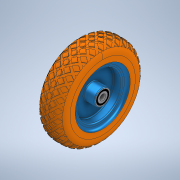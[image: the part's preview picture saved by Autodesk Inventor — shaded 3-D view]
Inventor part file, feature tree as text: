
AUTODESK INVENTOR PART (.ipt)
format: ipt  version: 2021 (Build 250183000, 183)  size: 4,260,352 bytes
history: native  units: mm
features: extrude x13, sketch x8, fillet x6, pattern_circular x2, plane x1
ambient origin geometry x8: Origin, YZ Plane, XZ Plane, XY Plane, X Axis, Y Axis, Z Axis, Center Point
bodies: Solid1 (feature_tree)
feature tree (30):
  sketch  "Sketch1"  dims[d2=70.0mm d3=0.0mm d4=8.0mm d5=0.0mm]
  extrude  "Extrusion1"  Depth=8.0mm TaperAngle=0.0deg
  extrude  "Extrusion2"  Depth=8.0mm TaperAngle=0.0deg
  extrude  "Extrusion3"  Depth=45.0mm
  sketch  "Sketch2"  dims[d6=30.0mm d7=0.0mm d8=8.0mm d9=0.0mm]
  extrude  "Extrusion4"  Depth=30.0mm TaperAngle=0.0deg
  extrude  "Extrusion5"  Depth=8.0mm
  extrude  "Extrusion6"  Depth=30.0mm
  extrude  "Extrusion7"  Depth=1.0mm
  fillet  "Fillet1"  Radius=40.0mm
  fillet  "Fillet2"  Radius=1.0mm
  fillet  "Fillet3"  Radius=27.0mm
  fillet  "Fillet4"  Radius=36.0mm
  extrude  "Extrusion8"  Depth=27.0mm
  fillet  "Fillet5"  Radius=36.0mm
  pattern_circular  "Circular Pattern1"  [2 undecoded]
  fillet  "Fillet6"  Radius=240.0mm
  extrude  "Extrusion9"  Depth=130.0mm
  extrude  "Extrusion10"  TaperAngle=45.0deg  [1 undecoded]
  plane  "Work Plane1"
  sketch  "Sketch8"  dims[d22=5.0mm d23=0.0mm d24=1.0mm d25=40.0mm d26=360.0deg d28=1.0mm d29=27.0mm d31=36.0mm]
  extrude  "Extrusion16"  Depth=2.0mm TaperAngle=0.0deg
  extrude  "Extrusion17"  Depth=2.0mm TaperAngle=0.0deg
  extrude  "Extrusion18"  Depth=2.0mm TaperAngle=0.0deg
  pattern_circular  "Circular Pattern5"  Count=30 Angle=360.0deg
  sketch  "Sketch11"  dims[d32=0.1mm d33=0.0mm d34=27.0mm d35=36.0mm d36=0.1mm d37=0.0mm d38=240.0mm d40=130.0mm d41=45.0deg d67=2.0mm d68=0.0mm d81=2.0mm d82=0.0mm d83=2.0mm d84=0.0mm d85=300.0mm d86=360.0deg]
  sketch  "Sketch4"  dims[d10=30.0mm d11=0.0mm d12=45.0mm]
  sketch  "Sketch5"  dims[d13=30.0mm d14=0.0mm d15=30.0mm d16=0.0mm]
  sketch  "Sketch6"  dims[d17=2.0mm d18=8.0mm]
  sketch  "Sketch7"  dims[d19=3.0mm d20=30.0mm]
note: 3 required parameter values undecoded (feature->parameter linkage not recoverable at this tier; creation-order binding heuristic only, values carry confidence <= 0.55)
